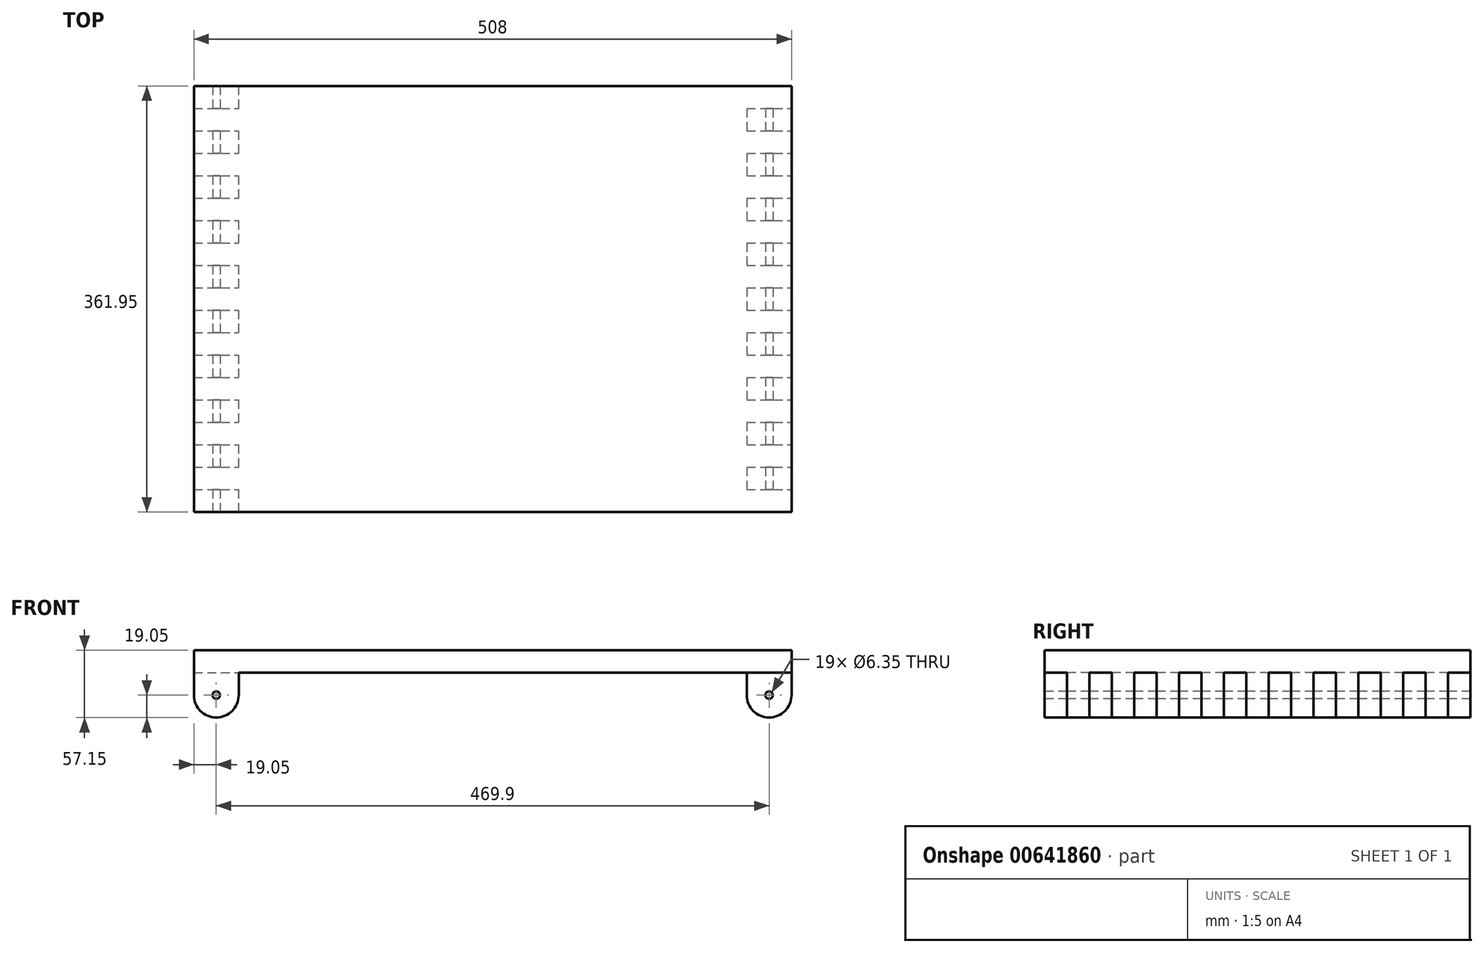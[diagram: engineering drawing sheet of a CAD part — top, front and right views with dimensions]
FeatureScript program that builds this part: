
annotation { "Feature Type Name" : "Feature", "Feature Type Description" : "" }
export const myFeature = defineFeature(function(context is Context, id is Id, definition is map)
    precondition{}
    {
        {
            var Q0;
            Q0=qCreatedBy(makeId("Top.planeOp"),FACE);
            var sketch = newSketch(context, id + "F0", { "sketchPlane" : qUnion([Q0])});
            skLineSegment(sketch, "E0.bottom", {"start": v(0, 0) * mm, "end": v(508, 0) * mm});
            skLineSegment(sketch, "E0.top", {"start": v(0, 361.95) * mm, "end": v(508, 361.95) * mm});
            skLineSegment(sketch, "E0.left", {"start": v(0, 0) * mm, "end": v(0, 361.95) * mm});
            skLineSegment(sketch, "E0.right", {"start": v(508, 0) * mm, "end": v(508, 361.95) * mm});
            skSolve(sketch);
        }
        {
            var Q0;
            Q0 = qSketchRegion(id + "F0", true);
            extrude(context, id + "F1", {"entities" : qUnion([Q0]), "depth" : 19.05 * mm, "offsetDistance" : 25.4 * mm});
        }
        {
            var Q0;
            Q0=makeQuery(id+"F1.opExtrude","CAP_FACE",FACE,{"disambiguationData":[OSD([sQuery(id+"F0.wireOp",EDGE,"E0.bottom"),sQuery(id+"F0.wireOp",EDGE,"E0.top"),sQuery(id+"F0.wireOp",EDGE,"E0.left"),sQuery(id+"F0.wireOp",EDGE,"E0.right")])],"isStart":true});
            var sketch = newSketch(context, id + "F2", { "sketchPlane" : qUnion([Q0])});
            skLineSegment(sketch, "E1.bottom", {"start": v(0, 0) * mm, "end": v(38.1, 0) * mm});
            skLineSegment(sketch, "E1.top", {"start": v(0, -19.05) * mm, "end": v(38.1, -19.05) * mm});
            skLineSegment(sketch, "E1.left", {"start": v(0, 0) * mm, "end": v(0, -19.05) * mm});
            skLineSegment(sketch, "E1.right", {"start": v(38.1, 0) * mm, "end": v(38.1, -19.05) * mm});
            skLineSegment(sketch, "E2.0.1.0", {"start": v(38.1, -38.1) * mm, "end": v(38.1, -57.15) * mm});
            skLineSegment(sketch, "E2.0.1.1", {"start": v(0, -38.1) * mm, "end": v(38.1, -38.1) * mm});
            skLineSegment(sketch, "E2.0.1.2", {"start": v(0, -38.1) * mm, "end": v(0, -57.15) * mm});
            skLineSegment(sketch, "E2.0.1.3", {"start": v(0, -57.15) * mm, "end": v(38.1, -57.15) * mm});
            skLineSegment(sketch, "E2.0.2.0", {"start": v(38.1, -76.2) * mm, "end": v(38.1, -95.25) * mm});
            skLineSegment(sketch, "E2.0.2.1", {"start": v(0, -76.2) * mm, "end": v(38.1, -76.2) * mm});
            skLineSegment(sketch, "E2.0.2.2", {"start": v(0, -76.2) * mm, "end": v(0, -95.25) * mm});
            skLineSegment(sketch, "E2.0.2.3", {"start": v(0, -95.25) * mm, "end": v(38.1, -95.25) * mm});
            skLineSegment(sketch, "E2.0.3.0", {"start": v(38.1, -114.3) * mm, "end": v(38.1, -133.35) * mm});
            skLineSegment(sketch, "E2.0.3.1", {"start": v(0, -114.3) * mm, "end": v(38.1, -114.3) * mm});
            skLineSegment(sketch, "E2.0.3.2", {"start": v(0, -114.3) * mm, "end": v(0, -133.35) * mm});
            skLineSegment(sketch, "E2.0.3.3", {"start": v(0, -133.35) * mm, "end": v(38.1, -133.35) * mm});
            skLineSegment(sketch, "E2.0.4.0", {"start": v(38.1, -152.4) * mm, "end": v(38.1, -171.45) * mm});
            skLineSegment(sketch, "E2.0.4.1", {"start": v(0, -152.4) * mm, "end": v(38.1, -152.4) * mm});
            skLineSegment(sketch, "E2.0.4.2", {"start": v(0, -152.4) * mm, "end": v(0, -171.45) * mm});
            skLineSegment(sketch, "E2.0.4.3", {"start": v(0, -171.45) * mm, "end": v(38.1, -171.45) * mm});
            skLineSegment(sketch, "E2.0.5.0", {"start": v(38.1, -190.5) * mm, "end": v(38.1, -209.55) * mm});
            skLineSegment(sketch, "E2.0.5.1", {"start": v(0, -190.5) * mm, "end": v(38.1, -190.5) * mm});
            skLineSegment(sketch, "E2.0.5.2", {"start": v(0, -190.5) * mm, "end": v(0, -209.55) * mm});
            skLineSegment(sketch, "E2.0.5.3", {"start": v(0, -209.55) * mm, "end": v(38.1, -209.55) * mm});
            skLineSegment(sketch, "E2.0.6.0", {"start": v(38.1, -228.6) * mm, "end": v(38.1, -247.65) * mm});
            skLineSegment(sketch, "E2.0.6.1", {"start": v(0, -228.6) * mm, "end": v(38.1, -228.6) * mm});
            skLineSegment(sketch, "E2.0.6.2", {"start": v(0, -228.6) * mm, "end": v(0, -247.65) * mm});
            skLineSegment(sketch, "E2.0.6.3", {"start": v(0, -247.65) * mm, "end": v(38.1, -247.65) * mm});
            skLineSegment(sketch, "E2.0.7.0", {"start": v(38.1, -266.7) * mm, "end": v(38.1, -285.75) * mm});
            skLineSegment(sketch, "E2.0.7.1", {"start": v(0, -266.7) * mm, "end": v(38.1, -266.7) * mm});
            skLineSegment(sketch, "E2.0.7.2", {"start": v(0, -266.7) * mm, "end": v(0, -285.75) * mm});
            skLineSegment(sketch, "E2.0.7.3", {"start": v(0, -285.75) * mm, "end": v(38.1, -285.75) * mm});
            skLineSegment(sketch, "E2.0.8.0", {"start": v(38.1, -304.8) * mm, "end": v(38.1, -323.85) * mm});
            skLineSegment(sketch, "E2.0.8.1", {"start": v(0, -304.8) * mm, "end": v(38.1, -304.8) * mm});
            skLineSegment(sketch, "E2.0.8.2", {"start": v(0, -304.8) * mm, "end": v(0, -323.85) * mm});
            skLineSegment(sketch, "E2.0.8.3", {"start": v(0, -323.85) * mm, "end": v(38.1, -323.85) * mm});
            skLineSegment(sketch, "E2.0.9.0", {"start": v(38.1, -342.9) * mm, "end": v(38.1, -361.95) * mm});
            skLineSegment(sketch, "E2.0.9.1", {"start": v(0, -342.9) * mm, "end": v(38.1, -342.9) * mm});
            skLineSegment(sketch, "E2.0.9.2", {"start": v(0, -342.9) * mm, "end": v(0, -361.95) * mm});
            skLineSegment(sketch, "E2.0.9.3", {"start": v(0, -361.95) * mm, "end": v(38.1, -361.95) * mm});
            skLineSegment(sketch, "E2.1.0.0", {"start": v(508, 0) * mm, "end": v(508, -19.05) * mm});
            skLineSegment(sketch, "E2.1.0.1", {"start": v(469.9, 0) * mm, "end": v(508, 0) * mm});
            skLineSegment(sketch, "E2.1.0.2", {"start": v(469.9, 0) * mm, "end": v(469.9, -19.05) * mm});
            skLineSegment(sketch, "E2.1.0.3", {"start": v(469.9, -19.05) * mm, "end": v(508, -19.05) * mm});
            skLineSegment(sketch, "E2.1.1.0", {"start": v(508, -38.1) * mm, "end": v(508, -57.15) * mm});
            skLineSegment(sketch, "E2.1.1.1", {"start": v(469.9, -38.1) * mm, "end": v(508, -38.1) * mm});
            skLineSegment(sketch, "E2.1.1.2", {"start": v(469.9, -38.1) * mm, "end": v(469.9, -57.15) * mm});
            skLineSegment(sketch, "E2.1.1.3", {"start": v(469.9, -57.15) * mm, "end": v(508, -57.15) * mm});
            skLineSegment(sketch, "E2.1.2.0", {"start": v(508, -76.2) * mm, "end": v(508, -95.25) * mm});
            skLineSegment(sketch, "E2.1.2.1", {"start": v(469.9, -76.2) * mm, "end": v(508, -76.2) * mm});
            skLineSegment(sketch, "E2.1.2.2", {"start": v(469.9, -76.2) * mm, "end": v(469.9, -95.25) * mm});
            skLineSegment(sketch, "E2.1.2.3", {"start": v(469.9, -95.25) * mm, "end": v(508, -95.25) * mm});
            skLineSegment(sketch, "E2.1.3.0", {"start": v(508, -114.3) * mm, "end": v(508, -133.35) * mm});
            skLineSegment(sketch, "E2.1.3.1", {"start": v(469.9, -114.3) * mm, "end": v(508, -114.3) * mm});
            skLineSegment(sketch, "E2.1.3.2", {"start": v(469.9, -114.3) * mm, "end": v(469.9, -133.35) * mm});
            skLineSegment(sketch, "E2.1.3.3", {"start": v(469.9, -133.35) * mm, "end": v(508, -133.35) * mm});
            skLineSegment(sketch, "E2.1.4.0", {"start": v(508, -152.4) * mm, "end": v(508, -171.45) * mm});
            skLineSegment(sketch, "E2.1.4.1", {"start": v(469.9, -152.4) * mm, "end": v(508, -152.4) * mm});
            skLineSegment(sketch, "E2.1.4.2", {"start": v(469.9, -152.4) * mm, "end": v(469.9, -171.45) * mm});
            skLineSegment(sketch, "E2.1.4.3", {"start": v(469.9, -171.45) * mm, "end": v(508, -171.45) * mm});
            skLineSegment(sketch, "E2.1.5.0", {"start": v(508, -190.5) * mm, "end": v(508, -209.55) * mm});
            skLineSegment(sketch, "E2.1.5.1", {"start": v(469.9, -190.5) * mm, "end": v(508, -190.5) * mm});
            skLineSegment(sketch, "E2.1.5.2", {"start": v(469.9, -190.5) * mm, "end": v(469.9, -209.55) * mm});
            skLineSegment(sketch, "E2.1.5.3", {"start": v(469.9, -209.55) * mm, "end": v(508, -209.55) * mm});
            skLineSegment(sketch, "E2.1.6.0", {"start": v(508, -228.6) * mm, "end": v(508, -247.65) * mm});
            skLineSegment(sketch, "E2.1.6.1", {"start": v(469.9, -228.6) * mm, "end": v(508, -228.6) * mm});
            skLineSegment(sketch, "E2.1.6.2", {"start": v(469.9, -228.6) * mm, "end": v(469.9, -247.65) * mm});
            skLineSegment(sketch, "E2.1.6.3", {"start": v(469.9, -247.65) * mm, "end": v(508, -247.65) * mm});
            skLineSegment(sketch, "E2.1.7.0", {"start": v(508, -266.7) * mm, "end": v(508, -285.75) * mm});
            skLineSegment(sketch, "E2.1.7.1", {"start": v(469.9, -266.7) * mm, "end": v(508, -266.7) * mm});
            skLineSegment(sketch, "E2.1.7.2", {"start": v(469.9, -266.7) * mm, "end": v(469.9, -285.75) * mm});
            skLineSegment(sketch, "E2.1.7.3", {"start": v(469.9, -285.75) * mm, "end": v(508, -285.75) * mm});
            skLineSegment(sketch, "E2.1.8.0", {"start": v(508, -304.8) * mm, "end": v(508, -323.85) * mm});
            skLineSegment(sketch, "E2.1.8.1", {"start": v(469.9, -304.8) * mm, "end": v(508, -304.8) * mm});
            skLineSegment(sketch, "E2.1.8.2", {"start": v(469.9, -304.8) * mm, "end": v(469.9, -323.85) * mm});
            skLineSegment(sketch, "E2.1.8.3", {"start": v(469.9, -323.85) * mm, "end": v(508, -323.85) * mm});
            skLineSegment(sketch, "E2.1.9.0", {"start": v(508, -342.9) * mm, "end": v(508, -361.95) * mm});
            skLineSegment(sketch, "E2.1.9.1", {"start": v(469.9, -342.9) * mm, "end": v(508, -342.9) * mm});
            skLineSegment(sketch, "E2.1.9.2", {"start": v(469.9, -342.9) * mm, "end": v(469.9, -361.95) * mm});
            skLineSegment(sketch, "E2.1.9.3", {"start": v(469.9, -361.95) * mm, "end": v(508, -361.95) * mm});
            skLineSegment(sketch, "E2.direction1", {"start": v(0, -19.05) * mm, "end": v(469.9, -19.05) * mm, "construction": true});
            skLineSegment(sketch, "E2.direction2", {"start": v(0, -19.05) * mm, "end": v(0, -57.15) * mm, "construction": true});
            skSolve(sketch);
        }
        {
            var Q0;
            Q0 = qSketchRegion(id + "F2", true);
            extrude(context, id + "F3", {"entities" : qUnion([Q0]), "operationType" : NewBodyOperationType.ADD, "depth" : 38.1 * mm, "offsetDistance" : 25.4 * mm});
        }
        {
            var Q0;
            Q0=makeQuery(id+"F3.opExtrude","CAP_EDGE",EDGE,{"disambiguationData":[OSD([sQuery(id+"F2.wireOp",EDGE,"E2.1.0.0")])],"isStart":false});
            var Q1;
            Q1=makeQuery(id+"F3.opExtrude","CAP_EDGE",EDGE,{"disambiguationData":[OSD([sQuery(id+"F2.wireOp",EDGE,"E2.1.0.2")])],"isStart":false});
            var Q2;
            Q2=makeQuery(id+"F3.opExtrude","CAP_EDGE",EDGE,{"disambiguationData":[OSD([sQuery(id+"F2.wireOp",EDGE,"E2.1.1.2")])],"isStart":false});
            var Q3;
            Q3=makeQuery(id+"F3.opExtrude","CAP_EDGE",EDGE,{"disambiguationData":[OSD([sQuery(id+"F2.wireOp",EDGE,"E2.1.1.0")])],"isStart":false});
            var Q4;
            Q4=makeQuery(id+"F3.opExtrude","CAP_EDGE",EDGE,{"disambiguationData":[OSD([sQuery(id+"F2.wireOp",EDGE,"E2.1.2.0")])],"isStart":false});
            var Q5;
            Q5=makeQuery(id+"F3.opExtrude","CAP_EDGE",EDGE,{"disambiguationData":[OSD([sQuery(id+"F2.wireOp",EDGE,"E2.1.2.2")])],"isStart":false});
            var Q6;
            Q6=makeQuery(id+"F3.opExtrude","CAP_EDGE",EDGE,{"disambiguationData":[OSD([sQuery(id+"F2.wireOp",EDGE,"E2.1.3.2")])],"isStart":false});
            var Q7;
            Q7=makeQuery(id+"F3.opExtrude","CAP_EDGE",EDGE,{"disambiguationData":[OSD([sQuery(id+"F2.wireOp",EDGE,"E2.1.3.0")])],"isStart":false});
            var Q8;
            Q8=makeQuery(id+"F3.opExtrude","CAP_EDGE",EDGE,{"disambiguationData":[OSD([sQuery(id+"F2.wireOp",EDGE,"E2.1.4.0")])],"isStart":false});
            var Q9;
            Q9=makeQuery(id+"F3.opExtrude","CAP_EDGE",EDGE,{"disambiguationData":[OSD([sQuery(id+"F2.wireOp",EDGE,"E2.1.4.2")])],"isStart":false});
            var Q10;
            Q10=makeQuery(id+"F3.opExtrude","CAP_EDGE",EDGE,{"disambiguationData":[OSD([sQuery(id+"F2.wireOp",EDGE,"E2.1.5.0")])],"isStart":false});
            var Q11;
            Q11=makeQuery(id+"F3.opExtrude","CAP_EDGE",EDGE,{"disambiguationData":[OSD([sQuery(id+"F2.wireOp",EDGE,"E2.1.5.2")])],"isStart":false});
            var Q12;
            Q12=makeQuery(id+"F3.opExtrude","CAP_EDGE",EDGE,{"disambiguationData":[OSD([sQuery(id+"F2.wireOp",EDGE,"E2.1.6.2")])],"isStart":false});
            var Q13;
            Q13=makeQuery(id+"F3.opExtrude","CAP_EDGE",EDGE,{"disambiguationData":[OSD([sQuery(id+"F2.wireOp",EDGE,"E2.1.6.0")])],"isStart":false});
            var Q14;
            Q14=makeQuery(id+"F3.opExtrude","CAP_EDGE",EDGE,{"disambiguationData":[OSD([sQuery(id+"F2.wireOp",EDGE,"E2.1.7.2")])],"isStart":false});
            var Q15;
            Q15=makeQuery(id+"F3.opExtrude","CAP_EDGE",EDGE,{"disambiguationData":[OSD([sQuery(id+"F2.wireOp",EDGE,"E2.1.7.0")])],"isStart":false});
            var Q16;
            Q16=makeQuery(id+"F3.opExtrude","CAP_EDGE",EDGE,{"disambiguationData":[OSD([sQuery(id+"F2.wireOp",EDGE,"E2.1.8.2")])],"isStart":false});
            var Q17;
            Q17=makeQuery(id+"F3.opExtrude","CAP_EDGE",EDGE,{"disambiguationData":[OSD([sQuery(id+"F2.wireOp",EDGE,"E2.1.8.0")])],"isStart":false});
            var Q18;
            Q18=makeQuery(id+"F3.opExtrude","CAP_EDGE",EDGE,{"disambiguationData":[OSD([sQuery(id+"F2.wireOp",EDGE,"E2.1.9.2")])],"isStart":false});
            var Q19;
            Q19=makeQuery(id+"F3.opExtrude","CAP_EDGE",EDGE,{"disambiguationData":[OSD([sQuery(id+"F2.wireOp",EDGE,"E2.1.9.0")])],"isStart":false});
            fillet(context, id + "F4", {"entities" : qUnion([Q0, Q1, Q2, Q3, Q4, Q5, Q6, Q7, Q8, Q9, Q10, Q11, Q12, Q13, Q14, Q15, Q16, Q17, Q18, Q19]), "radius" : 19.05 * mm, "tangentPropagation" : true, "allowEdgeOverflow" : false});
        }
        {
            var Q0;
            Q0=makeQuery(id+"F3.opExtrude","CAP_EDGE",EDGE,{"disambiguationData":[OSD([sQuery(id+"F2.wireOp",EDGE,"E1.right")])],"isStart":false});
            var Q1;
            Q1=makeQuery(id+"F3.opExtrude","CAP_EDGE",EDGE,{"disambiguationData":[OSD([sQuery(id+"F2.wireOp",EDGE,"E1.left")])],"isStart":false});
            var Q2;
            Q2=makeQuery(id+"F3.opExtrude","CAP_EDGE",EDGE,{"disambiguationData":[OSD([sQuery(id+"F2.wireOp",EDGE,"E2.0.1.0")])],"isStart":false});
            var Q3;
            Q3=makeQuery(id+"F3.opExtrude","CAP_EDGE",EDGE,{"disambiguationData":[OSD([sQuery(id+"F2.wireOp",EDGE,"E2.0.1.2")])],"isStart":false});
            var Q4;
            Q4=makeQuery(id+"F3.opExtrude","CAP_EDGE",EDGE,{"disambiguationData":[OSD([sQuery(id+"F2.wireOp",EDGE,"E2.0.2.0")])],"isStart":false});
            var Q5;
            Q5=makeQuery(id+"F3.opExtrude","CAP_EDGE",EDGE,{"disambiguationData":[OSD([sQuery(id+"F2.wireOp",EDGE,"E2.0.2.2")])],"isStart":false});
            var Q6;
            Q6=makeQuery(id+"F3.opExtrude","CAP_EDGE",EDGE,{"disambiguationData":[OSD([sQuery(id+"F2.wireOp",EDGE,"E2.0.3.0")])],"isStart":false});
            var Q7;
            Q7=makeQuery(id+"F3.opExtrude","CAP_EDGE",EDGE,{"disambiguationData":[OSD([sQuery(id+"F2.wireOp",EDGE,"E2.0.3.2")])],"isStart":false});
            var Q8;
            Q8=makeQuery(id+"F3.opExtrude","CAP_EDGE",EDGE,{"disambiguationData":[OSD([sQuery(id+"F2.wireOp",EDGE,"E2.0.4.2")])],"isStart":false});
            var Q9;
            Q9=makeQuery(id+"F3.opExtrude","CAP_EDGE",EDGE,{"disambiguationData":[OSD([sQuery(id+"F2.wireOp",EDGE,"E2.0.4.0")])],"isStart":false});
            var Q10;
            Q10=makeQuery(id+"F3.opExtrude","CAP_EDGE",EDGE,{"disambiguationData":[OSD([sQuery(id+"F2.wireOp",EDGE,"E2.0.5.0")])],"isStart":false});
            var Q11;
            Q11=makeQuery(id+"F3.opExtrude","CAP_EDGE",EDGE,{"disambiguationData":[OSD([sQuery(id+"F2.wireOp",EDGE,"E2.0.5.2")])],"isStart":false});
            var Q12;
            Q12=makeQuery(id+"F3.opExtrude","CAP_EDGE",EDGE,{"disambiguationData":[OSD([sQuery(id+"F2.wireOp",EDGE,"E2.0.6.2")])],"isStart":false});
            var Q13;
            Q13=makeQuery(id+"F3.opExtrude","CAP_EDGE",EDGE,{"disambiguationData":[OSD([sQuery(id+"F2.wireOp",EDGE,"E2.0.6.0")])],"isStart":false});
            var Q14;
            Q14=makeQuery(id+"F3.opExtrude","CAP_EDGE",EDGE,{"disambiguationData":[OSD([sQuery(id+"F2.wireOp",EDGE,"E2.0.7.0")])],"isStart":false});
            var Q15;
            Q15=makeQuery(id+"F3.opExtrude","CAP_EDGE",EDGE,{"disambiguationData":[OSD([sQuery(id+"F2.wireOp",EDGE,"E2.0.7.2")])],"isStart":false});
            var Q16;
            Q16=makeQuery(id+"F3.opExtrude","CAP_EDGE",EDGE,{"disambiguationData":[OSD([sQuery(id+"F2.wireOp",EDGE,"E2.0.8.0")])],"isStart":false});
            var Q17;
            Q17=makeQuery(id+"F3.opExtrude","CAP_EDGE",EDGE,{"disambiguationData":[OSD([sQuery(id+"F2.wireOp",EDGE,"E2.0.8.2")])],"isStart":false});
            var Q18;
            Q18=makeQuery(id+"F3.opExtrude","CAP_EDGE",EDGE,{"disambiguationData":[OSD([sQuery(id+"F2.wireOp",EDGE,"E2.0.9.0")])],"isStart":false});
            var Q19;
            Q19=makeQuery(id+"F3.opExtrude","CAP_EDGE",EDGE,{"disambiguationData":[OSD([sQuery(id+"F2.wireOp",EDGE,"E2.0.9.2")])],"isStart":false});
            fillet(context, id + "F5", {"entities" : qUnion([Q0, Q1, Q2, Q3, Q4, Q5, Q6, Q7, Q8, Q9, Q10, Q11, Q12, Q13, Q14, Q15, Q16, Q17, Q18, Q19]), "radius" : 19.05 * mm, "tangentPropagation" : true, "allowEdgeOverflow" : false});
        }
        {
            var Q0;
            Q0=makeQuery(id+"F3.boolean.opBoolean","MERGE",FACE,{"derivedFrom":[makeQuery(id+"F1.opExtrude","SWEPT_FACE",FACE,{"disambiguationData":[OSD([sQuery(id+"F0.wireOp",EDGE,"E0.bottom")])]}),makeQuery(id+"F3.opExtrude","SWEPT_FACE",FACE,{"disambiguationData":[OSD([sQuery(id+"F2.wireOp",EDGE,"E1.bottom")])]}),makeQuery(id+"F3.opExtrude","SWEPT_FACE",FACE,{"disambiguationData":[OSD([sQuery(id+"F2.wireOp",EDGE,"E2.1.0.1")])]})]});
            var sketch = newSketch(context, id + "F6", { "sketchPlane" : qUnion([Q0])});
            skCircle(sketch, "E3", {"center": v(19.05, -19.05) * mm, "radius": 3.18 * mm});
            skCircle(sketch, "E4", {"center": v(488.95, -19.05) * mm, "radius": 3.18 * mm});
            skSolve(sketch);
        }
        {
            var Q0;
            Q0 = qSketchRegion(id + "F6", true);
            extrude(context, id + "F7", {"entities" : qUnion([Q0]), "operationType" : NewBodyOperationType.REMOVE, "endBound" : BoundingType.THROUGH_ALL, "oppositeDirection" : true, "depth" : 25.4 * mm, "offsetDistance" : 25.4 * mm});
        }
        {
            var Q0;
            Q0=makeQuery(id+"F3.boolean.opBoolean","MERGE",FACE,{"derivedFrom":[makeQuery(id+"F1.opExtrude","SWEPT_FACE",FACE,{"disambiguationData":[OSD([sQuery(id+"F0.wireOp",EDGE,"E0.bottom")])]}),makeQuery(id+"F3.opExtrude","SWEPT_FACE",FACE,{"disambiguationData":[OSD([sQuery(id+"F2.wireOp",EDGE,"E1.bottom")])]}),makeQuery(id+"F3.opExtrude","SWEPT_FACE",FACE,{"disambiguationData":[OSD([sQuery(id+"F2.wireOp",EDGE,"E2.1.0.1")])]})]});
            var sketch = newSketch(context, id + "F8", { "sketchPlane" : qUnion([Q0])});
            skLineSegment(sketch, "E5.bottom", {"start": v(469.9, 0) * mm, "end": v(508, 0) * mm});
            skLineSegment(sketch, "E5.top", {"start": v(469.9, -38.1) * mm, "end": v(508, -38.1) * mm});
            skLineSegment(sketch, "E5.left", {"start": v(469.9, 0) * mm, "end": v(469.9, -38.1) * mm});
            skLineSegment(sketch, "E5.right", {"start": v(508, 0) * mm, "end": v(508, -38.1) * mm});
            skSolve(sketch);
        }
        {
            var Q0;
            Q0 = qSketchRegion(id + "F8", true);
            extrude(context, id + "F9", {"entities" : qUnion([Q0]), "operationType" : NewBodyOperationType.REMOVE, "endBound" : BoundingType.THROUGH_ALL, "oppositeDirection" : true, "depth" : 25.4 * mm, "offsetDistance" : 25.4 * mm});
        }
        {
            var Q0;
            Q0=makeQuery(id+"F9.boolean.opBoolean","MERGE",FACE,{"derivedFrom":[makeQuery(id+"F1.opExtrude","CAP_FACE",FACE,{"disambiguationData":[OSD([sQuery(id+"F0.wireOp",EDGE,"E0.bottom"),sQuery(id+"F0.wireOp",EDGE,"E0.top"),sQuery(id+"F0.wireOp",EDGE,"E0.left"),sQuery(id+"F0.wireOp",EDGE,"E0.right")])],"isStart":true}),makeQuery(id+"F9.opExtrude","SWEPT_FACE",FACE,{"disambiguationData":[OSD([sQuery(id+"F8.wireOp",EDGE,"E5.bottom")])]})]});
            var sketch = newSketch(context, id + "F10", { "sketchPlane" : qUnion([Q0])});
            skLineSegment(sketch, "E6.bottom", {"start": v(469.9, -38.1) * mm, "end": v(508, -38.1) * mm});
            skLineSegment(sketch, "E6.top", {"start": v(469.9, -19.05) * mm, "end": v(508, -19.05) * mm});
            skLineSegment(sketch, "E6.left", {"start": v(469.9, -38.1) * mm, "end": v(469.9, -19.05) * mm});
            skLineSegment(sketch, "E6.right", {"start": v(508, -38.1) * mm, "end": v(508, -19.05) * mm});
            skLineSegment(sketch, "E7.0.1.0", {"start": v(469.9, -57.15) * mm, "end": v(508, -57.15) * mm});
            skLineSegment(sketch, "E7.0.1.1", {"start": v(469.9, -76.2) * mm, "end": v(469.9, -57.15) * mm});
            skLineSegment(sketch, "E7.0.1.2", {"start": v(508, -76.2) * mm, "end": v(508, -57.15) * mm});
            skLineSegment(sketch, "E7.0.1.3", {"start": v(469.9, -76.2) * mm, "end": v(508, -76.2) * mm});
            skLineSegment(sketch, "E7.0.2.0", {"start": v(469.9, -95.25) * mm, "end": v(508, -95.25) * mm});
            skLineSegment(sketch, "E7.0.2.1", {"start": v(469.9, -114.3) * mm, "end": v(469.9, -95.25) * mm});
            skLineSegment(sketch, "E7.0.2.2", {"start": v(508, -114.3) * mm, "end": v(508, -95.25) * mm});
            skLineSegment(sketch, "E7.0.2.3", {"start": v(469.9, -114.3) * mm, "end": v(508, -114.3) * mm});
            skLineSegment(sketch, "E7.0.3.0", {"start": v(469.9, -133.35) * mm, "end": v(508, -133.35) * mm});
            skLineSegment(sketch, "E7.0.3.1", {"start": v(469.9, -152.4) * mm, "end": v(469.9, -133.35) * mm});
            skLineSegment(sketch, "E7.0.3.2", {"start": v(508, -152.4) * mm, "end": v(508, -133.35) * mm});
            skLineSegment(sketch, "E7.0.3.3", {"start": v(469.9, -152.4) * mm, "end": v(508, -152.4) * mm});
            skLineSegment(sketch, "E7.0.4.0", {"start": v(469.9, -171.45) * mm, "end": v(508, -171.45) * mm});
            skLineSegment(sketch, "E7.0.4.1", {"start": v(469.9, -190.5) * mm, "end": v(469.9, -171.45) * mm});
            skLineSegment(sketch, "E7.0.4.2", {"start": v(508, -190.5) * mm, "end": v(508, -171.45) * mm});
            skLineSegment(sketch, "E7.0.4.3", {"start": v(469.9, -190.5) * mm, "end": v(508, -190.5) * mm});
            skLineSegment(sketch, "E7.0.5.0", {"start": v(469.9, -209.55) * mm, "end": v(508, -209.55) * mm});
            skLineSegment(sketch, "E7.0.5.1", {"start": v(469.9, -228.6) * mm, "end": v(469.9, -209.55) * mm});
            skLineSegment(sketch, "E7.0.5.2", {"start": v(508, -228.6) * mm, "end": v(508, -209.55) * mm});
            skLineSegment(sketch, "E7.0.5.3", {"start": v(469.9, -228.6) * mm, "end": v(508, -228.6) * mm});
            skLineSegment(sketch, "E7.0.6.0", {"start": v(469.9, -247.65) * mm, "end": v(508, -247.65) * mm});
            skLineSegment(sketch, "E7.0.6.1", {"start": v(469.9, -266.7) * mm, "end": v(469.9, -247.65) * mm});
            skLineSegment(sketch, "E7.0.6.2", {"start": v(508, -266.7) * mm, "end": v(508, -247.65) * mm});
            skLineSegment(sketch, "E7.0.6.3", {"start": v(469.9, -266.7) * mm, "end": v(508, -266.7) * mm});
            skLineSegment(sketch, "E7.0.7.0", {"start": v(469.9, -285.75) * mm, "end": v(508, -285.75) * mm});
            skLineSegment(sketch, "E7.0.7.1", {"start": v(469.9, -304.8) * mm, "end": v(469.9, -285.75) * mm});
            skLineSegment(sketch, "E7.0.7.2", {"start": v(508, -304.8) * mm, "end": v(508, -285.75) * mm});
            skLineSegment(sketch, "E7.0.7.3", {"start": v(469.9, -304.8) * mm, "end": v(508, -304.8) * mm});
            skLineSegment(sketch, "E7.0.8.0", {"start": v(469.9, -323.85) * mm, "end": v(508, -323.85) * mm});
            skLineSegment(sketch, "E7.0.8.1", {"start": v(469.9, -342.9) * mm, "end": v(469.9, -323.85) * mm});
            skLineSegment(sketch, "E7.0.8.2", {"start": v(508, -342.9) * mm, "end": v(508, -323.85) * mm});
            skLineSegment(sketch, "E7.0.8.3", {"start": v(469.9, -342.9) * mm, "end": v(508, -342.9) * mm});
            skLineSegment(sketch, "E7.direction1", {"start": v(469.9, -38.1) * mm, "end": v(495.3, -38.1) * mm, "construction": true});
            skLineSegment(sketch, "E7.direction2", {"start": v(469.9, -38.1) * mm, "end": v(469.9, -76.2) * mm, "construction": true});
            skSolve(sketch);
        }
        {
            var Q0;
            Q0 = qSketchRegion(id + "F10", true);
            extrude(context, id + "F11", {"entities" : qUnion([Q0]), "operationType" : NewBodyOperationType.ADD, "depth" : 38.1 * mm, "offsetDistance" : 25.4 * mm});
        }
        {
            var Q0;
            Q0=makeQuery(id+"F11.opExtrude","CAP_EDGE",EDGE,{"disambiguationData":[OSD([sQuery(id+"F10.wireOp",EDGE,"E6.left")])],"isStart":false});
            var Q1;
            Q1=makeQuery(id+"F11.opExtrude","CAP_EDGE",EDGE,{"disambiguationData":[OSD([sQuery(id+"F10.wireOp",EDGE,"E6.right")])],"isStart":false});
            var Q2;
            Q2=makeQuery(id+"F11.opExtrude","CAP_EDGE",EDGE,{"disambiguationData":[OSD([sQuery(id+"F10.wireOp",EDGE,"E7.0.1.2")])],"isStart":false});
            var Q3;
            Q3=makeQuery(id+"F11.opExtrude","CAP_EDGE",EDGE,{"disambiguationData":[OSD([sQuery(id+"F10.wireOp",EDGE,"E7.0.2.2")])],"isStart":false});
            var Q4;
            Q4=makeQuery(id+"F11.opExtrude","CAP_EDGE",EDGE,{"disambiguationData":[OSD([sQuery(id+"F10.wireOp",EDGE,"E7.0.3.2")])],"isStart":false});
            var Q5;
            Q5=makeQuery(id+"F11.opExtrude","CAP_EDGE",EDGE,{"disambiguationData":[OSD([sQuery(id+"F10.wireOp",EDGE,"E7.0.4.2")])],"isStart":false});
            var Q6;
            Q6=makeQuery(id+"F11.opExtrude","CAP_EDGE",EDGE,{"disambiguationData":[OSD([sQuery(id+"F10.wireOp",EDGE,"E7.0.1.1")])],"isStart":false});
            var Q7;
            Q7=makeQuery(id+"F11.opExtrude","CAP_EDGE",EDGE,{"disambiguationData":[OSD([sQuery(id+"F10.wireOp",EDGE,"E7.0.2.1")])],"isStart":false});
            var Q8;
            Q8=makeQuery(id+"F11.opExtrude","CAP_EDGE",EDGE,{"disambiguationData":[OSD([sQuery(id+"F10.wireOp",EDGE,"E7.0.3.1")])],"isStart":false});
            var Q9;
            Q9=makeQuery(id+"F11.opExtrude","CAP_EDGE",EDGE,{"disambiguationData":[OSD([sQuery(id+"F10.wireOp",EDGE,"E7.0.4.1")])],"isStart":false});
            var Q10;
            Q10=makeQuery(id+"F11.opExtrude","CAP_EDGE",EDGE,{"disambiguationData":[OSD([sQuery(id+"F10.wireOp",EDGE,"E7.0.5.1")])],"isStart":false});
            var Q11;
            Q11=makeQuery(id+"F11.opExtrude","CAP_EDGE",EDGE,{"disambiguationData":[OSD([sQuery(id+"F10.wireOp",EDGE,"E7.0.6.1")])],"isStart":false});
            var Q12;
            Q12=makeQuery(id+"F11.opExtrude","CAP_EDGE",EDGE,{"disambiguationData":[OSD([sQuery(id+"F10.wireOp",EDGE,"E7.0.7.1")])],"isStart":false});
            var Q13;
            Q13=makeQuery(id+"F11.opExtrude","CAP_EDGE",EDGE,{"disambiguationData":[OSD([sQuery(id+"F10.wireOp",EDGE,"E7.0.8.1")])],"isStart":false});
            var Q14;
            Q14=makeQuery(id+"F11.opExtrude","CAP_EDGE",EDGE,{"disambiguationData":[OSD([sQuery(id+"F10.wireOp",EDGE,"E7.0.8.2")])],"isStart":false});
            var Q15;
            Q15=makeQuery(id+"F11.opExtrude","CAP_EDGE",EDGE,{"disambiguationData":[OSD([sQuery(id+"F10.wireOp",EDGE,"E7.0.7.2")])],"isStart":false});
            var Q16;
            Q16=makeQuery(id+"F11.opExtrude","CAP_EDGE",EDGE,{"disambiguationData":[OSD([sQuery(id+"F10.wireOp",EDGE,"E7.0.5.2")])],"isStart":false});
            var Q17;
            Q17=makeQuery(id+"F11.opExtrude","CAP_EDGE",EDGE,{"disambiguationData":[OSD([sQuery(id+"F10.wireOp",EDGE,"E7.0.6.2")])],"isStart":false});
            fillet(context, id + "F12", {"entities" : qUnion([Q0, Q1, Q2, Q3, Q4, Q5, Q6, Q7, Q8, Q9, Q10, Q11, Q12, Q13, Q14, Q15, Q16, Q17]), "radius" : 19.05 * mm, "tangentPropagation" : true, "allowEdgeOverflow" : false});
        }
        {
            var Q0;
            Q0=makeQuery(id+"F11.opExtrude","SWEPT_FACE",FACE,{"disambiguationData":[OSD([sQuery(id+"F10.wireOp",EDGE,"E6.top")])]});
            var sketch = newSketch(context, id + "F13", { "sketchPlane" : qUnion([Q0])});
            skCircle(sketch, "E8", {"center": v(488.95, -19.05) * mm, "radius": 3.18 * mm});
            skSolve(sketch);
        }
        {
            var Q0;
            Q0 = qSketchRegion(id + "F13", true);
            extrude(context, id + "F14", {"entities" : qUnion([Q0]), "operationType" : NewBodyOperationType.REMOVE, "endBound" : BoundingType.THROUGH_ALL, "oppositeDirection" : true, "depth" : 25.4 * mm, "offsetDistance" : 25.4 * mm});
        }
    });
